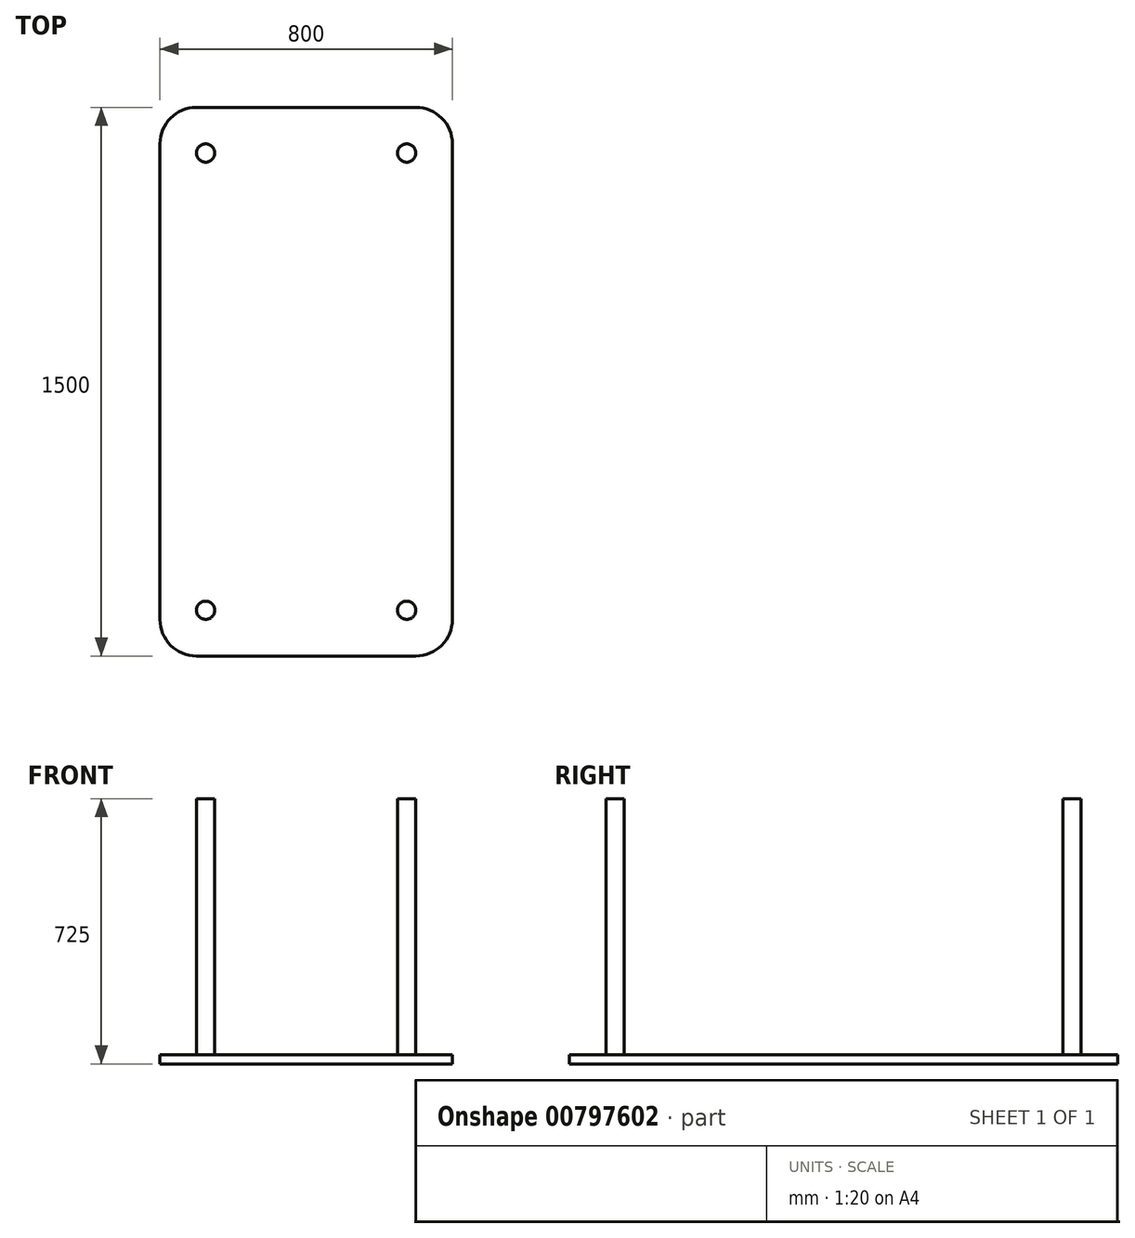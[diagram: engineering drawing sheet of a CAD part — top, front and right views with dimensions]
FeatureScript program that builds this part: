
annotation { "Feature Type Name" : "Feature", "Feature Type Description" : "" }
export const myFeature = defineFeature(function(context is Context, id is Id, definition is map)
    precondition{}
    {
        {
            var Q0;
            Q0=qCreatedBy(makeId("Top.planeOp"),FACE);
            var sketch = newSketch(context, id + "F0", { "sketchPlane" : qUnion([Q0])});
            skLineSegment(sketch, "E0.bottom", {"start": v(-400, 750) * mm, "end": v(400, 750) * mm});
            skLineSegment(sketch, "E0.top", {"start": v(-400, -750) * mm, "end": v(400, -750) * mm});
            skLineSegment(sketch, "E0.left", {"start": v(-400, 750) * mm, "end": v(-400, -750) * mm});
            skLineSegment(sketch, "E0.right", {"start": v(400, 750) * mm, "end": v(400, -750) * mm});
            skLineSegment(sketch, "E1", {"start": v(-400, -750) * mm, "end": v(400, 750) * mm, "construction": true});
            skSolve(sketch);
        }
        {
            var Q0;
            Q0=makeQuery(id+"F0.imprint","IMPRINT",FACE,{"disambiguationData":[TD([[makeQuery(id+"F0.imprint","IMPRINT",EDGE,{"derivedFrom":sQuery(id+"F0.wireOp",EDGE,"E0.bottom")}),-1.0]])]});
            extrude(context, id + "F1", {"entities" : qUnion([Q0]), "depth" : 25 * mm, "offsetDistance" : 25 * mm});
        }
        {
            var Q0;
            Q0=makeQuery(id+"F1.opExtrude","CAP_FACE",FACE,{"disambiguationData":[OSD([sQuery(id+"F0.wireOp",EDGE,"E0.bottom"),sQuery(id+"F0.wireOp",EDGE,"E0.top"),sQuery(id+"F0.wireOp",EDGE,"E0.left"),sQuery(id+"F0.wireOp",EDGE,"E0.right")])],"isStart":false});
            var sketch = newSketch(context, id + "F2", { "sketchPlane" : qUnion([Q0])});
            skCircle(sketch, "E2", {"center": v(-275, 625) * mm, "radius": 25 * mm});
            skLineSegment(sketch, "E3", {"start": v(-275, 625) * mm, "end": v(-275, 750) * mm, "construction": true});
            skLineSegment(sketch, "E4", {"start": v(-275, 625) * mm, "end": v(-400, 625) * mm, "construction": true});
            skSolve(sketch);
        }
        {
            var Q0;
            Q0=makeQuery(id+"F2.imprint","IMPRINT",FACE,{"disambiguationData":[TD([[makeQuery(id+"F2.imprint","IMPRINT",EDGE,{"derivedFrom":sQuery(id+"F2.wireOp",EDGE,"E2")}),1.0]])]});
            extrude(context, id + "F3", {"entities" : qUnion([Q0]), "depth" : 700 * mm, "offsetDistance" : 25 * mm});
        }
        {
            var Q0;
            Q0=makeQuery(id+"F3.opExtrude","SWEPT_BODY",BODY,{"disambiguationData":[OSD([sQuery(id+"F2.wireOp",EDGE,"E2")])]});
            var Q1;
            Q1=qCreatedBy(makeId("Front.planeOp"),FACE);
            mirror(context, id + "F4", {"entities" : qUnion([Q0]), "mirrorPlane" : qUnion([Q1])});
        }
        {
            var Q0;
            Q0=makeQuery(id+"F3.opExtrude","SWEPT_BODY",BODY,{"disambiguationData":[OSD([sQuery(id+"F2.wireOp",EDGE,"E2")])]});
            var Q1;
            Q1=makeQuery(id+"F4.opPattern","COPY",BODY,{"derivedFrom":makeQuery(id+"F3.opExtrude","SWEPT_BODY",BODY,{"disambiguationData":[OSD([sQuery(id+"F2.wireOp",EDGE,"E2")])]}),"instanceName":"1"});
            var Q2;
            Q2=qCreatedBy(makeId("Right.planeOp"),FACE);
            mirror(context, id + "F5", {"operationType" : NewBodyOperationType.ADD, "entities" : qUnion([Q0, Q1]), "mirrorPlane" : qUnion([Q2])});
        }
        {
            var Q0;
            Q0=makeQuery(id+"F1.opExtrude","SWEPT_EDGE",EDGE,{"disambiguationData":[OSD([sQuery(id+"F0.wireOp",EDGE,"E0.bottom"),sQuery(id+"F0.wireOp",EDGE,"E0.left")])]});
            var Q1;
            Q1=makeQuery(id+"F1.opExtrude","SWEPT_EDGE",EDGE,{"disambiguationData":[OSD([sQuery(id+"F0.wireOp",EDGE,"E0.bottom"),sQuery(id+"F0.wireOp",EDGE,"E0.right")])]});
            var Q2;
            Q2=makeQuery(id+"F1.opExtrude","SWEPT_EDGE",EDGE,{"disambiguationData":[OSD([sQuery(id+"F0.wireOp",EDGE,"E0.top"),sQuery(id+"F0.wireOp",EDGE,"E0.right")])]});
            var Q3;
            Q3=makeQuery(id+"F1.opExtrude","SWEPT_EDGE",EDGE,{"disambiguationData":[OSD([sQuery(id+"F0.wireOp",EDGE,"E0.top"),sQuery(id+"F0.wireOp",EDGE,"E0.left")])]});
            fillet(context, id + "F6", {"entities" : qUnion([Q0, Q1, Q2, Q3]), "radius" : 100 * mm, "tangentPropagation" : true, "allowEdgeOverflow" : false});
        }
    });
